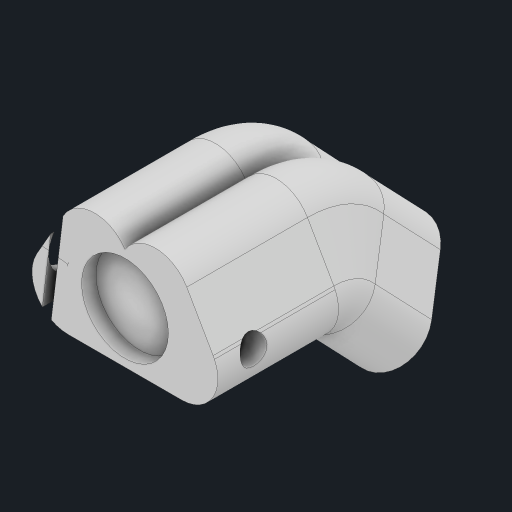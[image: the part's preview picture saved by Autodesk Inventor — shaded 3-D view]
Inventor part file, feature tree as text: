
AUTODESK INVENTOR PART (.ipt)
format: ipt  version: 2023 (Build 270158000, 158)  size: 513,024 bytes
history: native  units: mm
features: extrude x13, sketch x9, plane x3, chamfer x2, mirror x1, revolve x1
ambient origin geometry x8: Origin, YZ Plane, XZ Plane, XY Plane, X Axis, Y Axis, Z Axis, Center Point
bodies: Solid1 (feature_tree)
feature tree (29):
  sketch  "Sketch1"  dims[d0=100.0mm d1=25.0mm d2=7.5mm d3=7.5mm d4=60.0deg d5=15.0mm d6=11.0mm d7=11.0mm d8=15.0mm d14=4.0mm d15=0.0mm]
  extrude  "Extrusion1"  Depth=7.5mm TaperAngle=0.0deg
  plane  "Work Plane13"
  sketch  "Sketch7"  dims[d72=7.5mm d73=90.0deg]
  extrude  "Extrusion6"  TaperAngle=90.0deg  [1 undecoded]
  extrude  "Extrusion7"  Depth=7.5mm
  mirror  "Mirror4"
  plane  "Work Plane9"
  extrude  "Extrusion8"  Depth=15.0mm
  revolve  "Revolution2"  [1 undecoded]
  extrude  "Extrusion9"  Depth=6.5mm
  extrude  "Extrusion10"  Depth=15.0mm TaperAngle=0.0deg
  extrude  "Extrusion11"  Depth=10.0mm TaperAngle=0.0deg
  chamfer  "Chamfer3"  Distance=4.0mm
  chamfer  "Chamfer4"  Distance=10.0mm
  plane  "Work Plane16"
  extrude  "Extrusion14"  Depth=10.0mm TaperAngle=0.0deg
  extrude  "Extrusion15"  Depth=10.0mm TaperAngle=45.0deg
  sketch  "Sketch32"  dims[d93=10.0mm d94=0.0mm d115=20.0mm d116=0.0mm]
  extrude  "Extrusion21"  Depth=10.0mm TaperAngle=45.0deg
  extrude  "Extrusion22"  Depth=10.0mm
  extrude  "Extrusion23"  Depth=10.0mm
  extrude  "Extrusion25"  Depth=10.0mm
  sketch  "Sketch14"  dims[d74=7.5mm d75=5.5mm]
  sketch  "Sketch15"  dims[d76=5.5mm d77=15.0mm]
  sketch  "Sketch19"  dims[d78=11.0mm d79=11.0mm]
  sketch  "Sketch23"  dims[d80=2.0mm d81=6.5mm]
  sketch  "Sketch24"  dims[d82=6.5mm d83=15.0mm d84=0.0mm]
  sketch  "Sketch34"  dims[d131=8.648979mm d132=4.0mm d133=0.0mm d134=10.0mm d135=0.0mm d136=10.0mm d137=0.0mm d138=2.0mm d139=4.0mm d140=45.0deg d141=2.0mm d142=4.0mm d143=45.0deg d153=15.0mm d154=15.0mm d155=15.0mm d156=25.0mm d157=0.0mm d158=20.0mm d160=20.0mm d161=10.0mm d168=30.0mm d169=0.0mm d173=2.0mm d221=10.93871mm d243=1.21824mm d247=15.0mm d248=20.0mm d249=15.0mm d250=15.0mm d251=15.0mm d252=5.5mm d253=20.0mm d254=0.0mm d255=2.0mm d256=0.0mm d257=50.0mm d258=0.0mm d266=90.0deg d267=18.0mm d268=3.0mm d269=0.0mm d182=0.5mm d183=0.872665mm d184=0.5mm d185=0.872665mm d224=0.5mm d225=0.872665mm d226=0.5mm d227=0.872665mm]
note: 2 required parameter values undecoded (feature->parameter linkage not recoverable at this tier; creation-order binding heuristic only, values carry confidence <= 0.55)